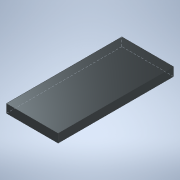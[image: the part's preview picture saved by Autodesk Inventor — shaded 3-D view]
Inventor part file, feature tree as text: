
AUTODESK INVENTOR PART (.ipt)
format: ipt  version: 2020 (Build 240168000, 168)  size: 93,696 bytes
history: native  units: mm
features: extrude x1, sketch x1
ambient origin geometry x8: Origin, YZ Plane, XZ Plane, XY Plane, X Axis, Y Axis, Z Axis, Center Point
bodies: Solid1 (feature_tree)
feature tree (2):
  extrude  "Extrusion1"  Depth=4.48mm TaperAngle=0.0deg
  sketch  "Sketch1"  dims[d0=27.3mm d1=4.48mm d2=0.0mm]
